# Revit family: HERZ Strömax Commissioning Valve With Test Points, Inclined Body 4218 GF PN16
name_source: partatom
category: Rohrzubehör
units: mm (PartAtom-declared; Revit-internal decimal feet)

## family parameters
Arbeitsebenenbasiert = Nein
Beim Laden mit Abzugskörper schneiden = Nein
Bemaßung runder Anschluss = Durchmesser verwenden
Gemeinsam genutzt = Nein
Immer vertikal = Ja
OmniClass-Nummer = 23.65.55.14
OmniClass-Titel = Valves for Liquid Services
Teiletyp = Unterbricht

## types (1)
- HERZ Strömax Commissioning Valve With Test Points, Inclined Body 4218 GF PN16
    Body = ductile iron EN-GJS-400-15
    Counting device = plastic material
    D05 = 75 mm  [stored 0.246063 ft]
    Differential pressure measurement = The STRÖMAX GF double regulating and commissioning valve is equipped with two measuring valves:
It is possible to measure the differential pressure with suitable measuring devices and to determine the flow rate accordingly.
    Field of application = For hydraulic balancing in heating or cooling systems, regulating and shutting off distribution circuits, heat exchangers, heating and cooling terminals.
    GT = 10 mm  [stored 0.0328084 ft]
    H06 = 27 mm
    H07 = 50 mm
    H08 = 47 mm
    H11 = 85 mm
    Hersteller = HERZ Armaturen Ges.m.b.H.
    Max. operating pressure = 1600000.0 Pa
    Max. operating temperature = 110 °C
    Medium = Heating water quality according to ÖNORM H 5195 or VDI guideline 2035.
Ethylene and propylene glycol can be used in a ratio of 25-50 vol. [%] are mixed.
    Min. operating temperature = -10 °C
    Model = STRÖMAX GF double regulating and commissioning valve with measuring valves, DN 350-500:
body nodular cast iron GJS 400-15 according to EN 1561, flange according to EN 1092, PN 16 or PN 25, blue enamel.
Valve upper part nodular cast iron GJS 400-15, with non-rising spindle, spindle sealing by means of a triple O-ring.
Presetting steps are displayed digitally.
    O-Ring = EPDM
    Regulating spindle = stainless steell
    SCRNCODE = 05;07;02
    SCRNSEQ = ARM;ARM_TYP="STRV";2
    Spindle = stainless steell
    URL = www.herzvalves.com
    Upper part = ductile iron EN-GJS-400-15
    Valve cone = ductile iron EN-GJS-400-15 according to EN 1561 / EPDM coated
    W01 = 50.00°
    W02 = 60.00°

note: [stored X ft] marks values corroborated as IEEE doubles in the binary element streams (Revit-internal decimal feet)
